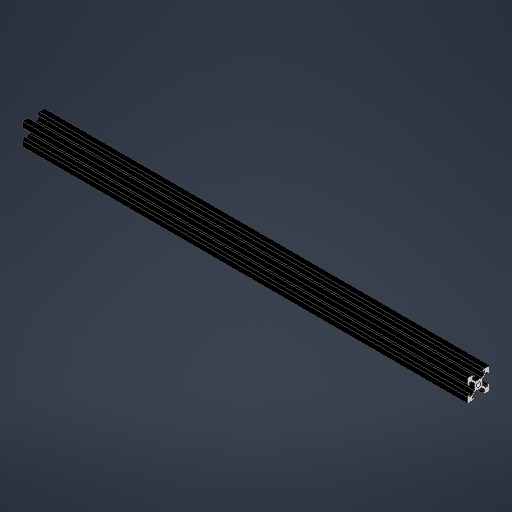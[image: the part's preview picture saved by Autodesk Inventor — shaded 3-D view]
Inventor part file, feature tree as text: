
AUTODESK INVENTOR PART (.ipt)
format: ipt  version: 2025.1 (Build 291241000, 241)  size: 270,336 bytes
history: native  units: mm
features: sketch x2, extrude x1
ambient origin geometry x8: Origin, YZ Plane, XZ Plane, XY Plane, X Axis, Y Axis, Z Axis, Center Point
bodies: Solid1 (feature_tree)
feature tree (3):
  extrude  "Extrusion1"  Depth=19.9mm
  sketch  "Sketch1"  dims[d0=19.9mm d1=19.9mm]
  sketch  "Sketch Circular Pattern1"  dims[d2=1.8mm d3=6.25mm d4=5.7mm d5=0.75mm d6=45.0deg d7=4.0mm d8=1.8mm d9=45.0deg d10=1.65mm d11=40.0mm d13=360.0deg d15=400.0mm d16=0.0mm]
